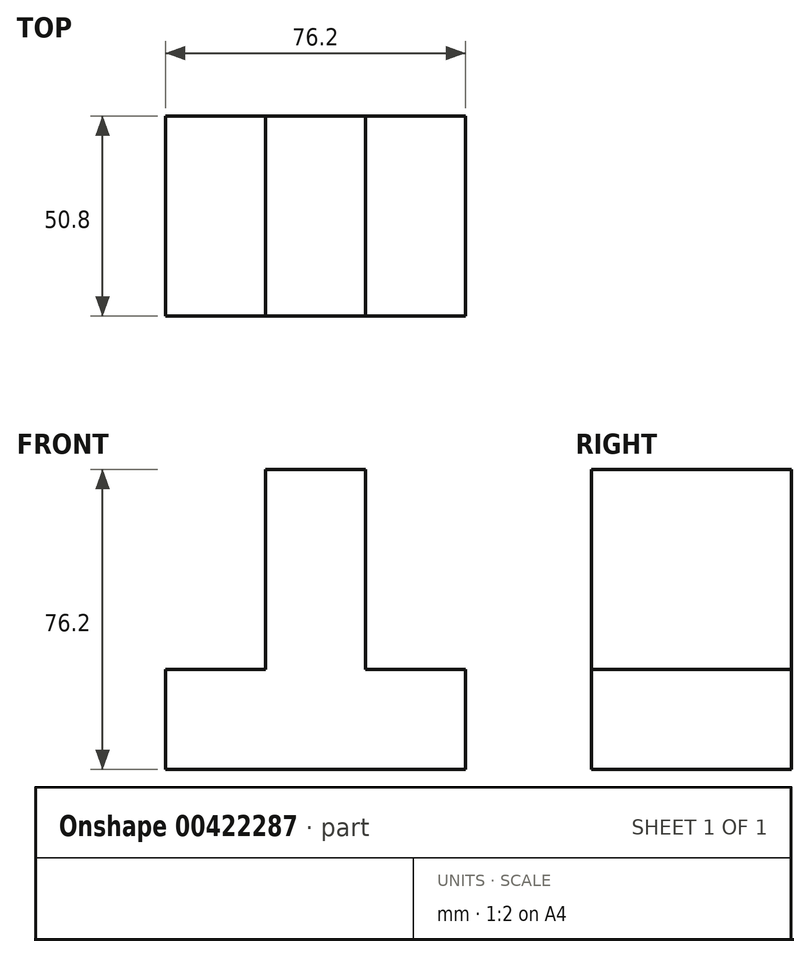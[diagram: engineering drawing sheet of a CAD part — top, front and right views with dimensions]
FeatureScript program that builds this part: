
annotation { "Feature Type Name" : "Feature", "Feature Type Description" : "" }
export const myFeature = defineFeature(function(context is Context, id is Id, definition is map)
    precondition{}
    {
        {
            var Q0;
            Q0=qCreatedBy(makeId("Front.planeOp"),FACE);
            var sketch = newSketch(context, id + "F0", { "sketchPlane" : qUnion([Q0])});
            skLineSegment(sketch, "E0", {"start": v(-59.07, -6.46) * mm, "end": v(-59.07, -31.86) * mm});
            skLineSegment(sketch, "E1", {"start": v(-59.07, -31.86) * mm, "end": v(17.13, -31.86) * mm});
            skLineSegment(sketch, "E2", {"start": v(17.13, -31.86) * mm, "end": v(17.13, -6.46) * mm});
            skLineSegment(sketch, "E3", {"start": v(17.13, -6.46) * mm, "end": v(-8.27, -6.46) * mm});
            skLineSegment(sketch, "E4", {"start": v(-59.07, -6.46) * mm, "end": v(-33.67, -6.46) * mm});
            skLineSegment(sketch, "E5", {"start": v(-33.67, -6.46) * mm, "end": v(-33.67, 44.34) * mm});
            skLineSegment(sketch, "E6", {"start": v(-8.27, -6.46) * mm, "end": v(-8.27, 44.34) * mm});
            skLineSegment(sketch, "E7", {"start": v(-33.67, 44.34) * mm, "end": v(-8.27, 44.34) * mm});
            skSolve(sketch);
        }
        {
            var Q0;
            Q0 = qSketchRegion(id + "F0", true);
            extrude(context, id + "F1", {"entities" : qUnion([Q0]), "depth" : 50.8 * mm});
        }
    });
